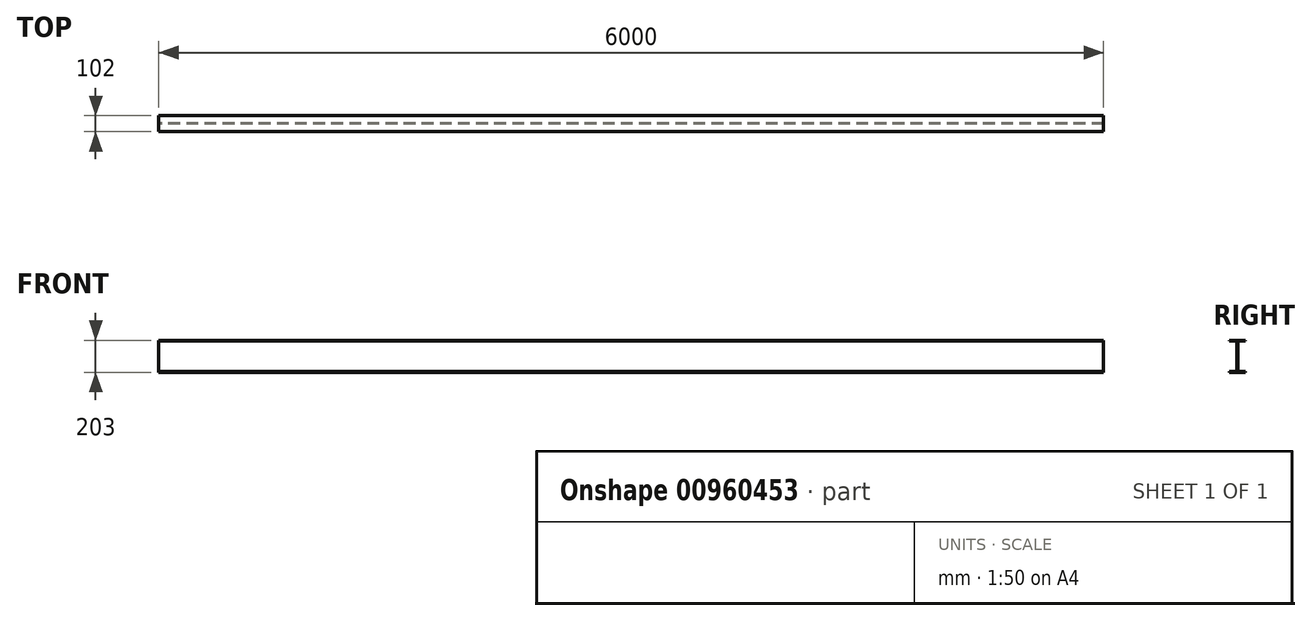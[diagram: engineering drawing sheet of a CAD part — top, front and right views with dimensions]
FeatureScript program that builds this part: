
annotation { "Feature Type Name" : "Feature", "Feature Type Description" : "" }
export const myFeature = defineFeature(function(context is Context, id is Id, definition is map)
    precondition{}
    {
        {
            var Q0;
            Q0=qCreatedBy(makeId("Right.planeOp"),FACE);
            var sketch = newSketch(context, id + "F0", { "sketchPlane" : qUnion([Q0])});
            skLineSegment(sketch, "E0.bottom", {"start": v(51, 101.5) * mm, "end": v(-51, 101.5) * mm});
            skLineSegment(sketch, "E0.top", {"start": v(51, -101.5) * mm, "end": v(-51, -101.5) * mm});
            skLineSegment(sketch, "E0.left", {"start": v(51, 101.5) * mm, "end": v(51, 96.5) * mm});
            skLineSegment(sketch, "E0.right", {"start": v(-51, 101.5) * mm, "end": v(-51, 96.5) * mm});
            skPoint(sketch, "E0.middle", {"position": v(0, 0) * mm});
            skLineSegment(sketch, "E1.0", {"start": v(51, 96.5) * mm, "end": v(2.5, 96.5) * mm});
            skLineSegment(sketch, "E2.0", {"start": v(51, -96.5) * mm, "end": v(2.5, -96.5) * mm});
            skLineSegment(sketch, "E3.0", {"start": v(-2.5, 96.5) * mm, "end": v(-2.5, -96.5) * mm});
            skLineSegment(sketch, "E4.0", {"start": v(2.5, 96.5) * mm, "end": v(2.5, -96.5) * mm});
            skLineSegment(sketch, "E5.trimOffspring", {"start": v(-2.5, 96.5) * mm, "end": v(-51, 96.5) * mm});
            skLineSegment(sketch, "E6.trimOffspring", {"start": v(-51, -96.5) * mm, "end": v(-51, -101.5) * mm});
            skLineSegment(sketch, "E7.trimOffspring", {"start": v(51, -96.5) * mm, "end": v(51, -101.5) * mm});
            skLineSegment(sketch, "E8.trimOffspring", {"start": v(-2.5, -96.5) * mm, "end": v(-51, -96.5) * mm});
            skSolve(sketch);
        }
        {
            var Q0;
            Q0=makeQuery(id+"F0.imprint","IMPRINT",FACE,{"disambiguationData":[TD([[makeQuery(id+"F0.imprint","IMPRINT",EDGE,{"derivedFrom":sQuery(id+"F0.wireOp",EDGE,"E0.bottom")}),1.0]])]});
            extrude(context, id + "F1", {"entities" : qUnion([Q0]), "endBound" : BoundingType.SYMMETRIC, "depth" : 6000 * mm, "offsetDistance" : 25 * mm});
        }
    });
